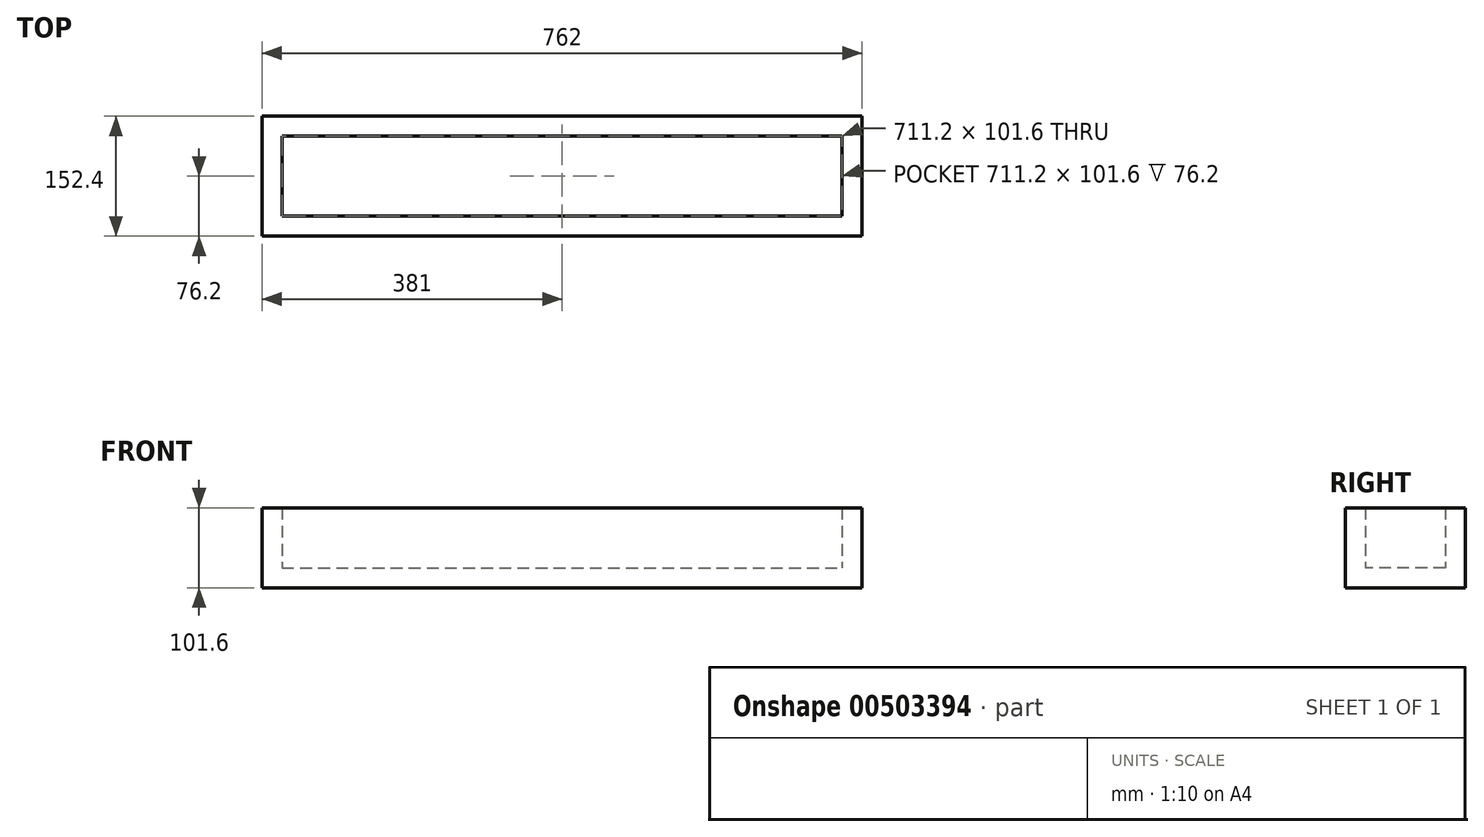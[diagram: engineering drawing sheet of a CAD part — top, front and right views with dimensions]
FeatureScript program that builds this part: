
annotation { "Feature Type Name" : "Feature", "Feature Type Description" : "" }
export const myFeature = defineFeature(function(context is Context, id is Id, definition is map)
    precondition{}
    {
        {
            var Q0;
            Q0=qCreatedBy(makeId("Top.planeOp"),FACE);
            var sketch = newSketch(context, id + "F0", { "sketchPlane" : qUnion([Q0])});
            skLineSegment(sketch, "E0.bottom", {"start": v(-381, 76.2) * mm, "end": v(381, 76.2) * mm});
            skLineSegment(sketch, "E0.top", {"start": v(-381, -76.2) * mm, "end": v(381, -76.2) * mm});
            skLineSegment(sketch, "E0.left", {"start": v(-381, 76.2) * mm, "end": v(-381, -76.2) * mm});
            skLineSegment(sketch, "E0.right", {"start": v(381, 76.2) * mm, "end": v(381, -76.2) * mm});
            skLineSegment(sketch, "E1", {"start": v(-381, 0) * mm, "end": v(381, 0) * mm, "construction": true});
            skSolve(sketch);
        }
        {
            var Q0;
            Q0 = qSketchRegion(id + "F0", true);
            extrude(context, id + "F1", {"entities" : qUnion([Q0]), "depth" : 101.6 * mm});
        }
        {
            var Q0;
            Q0=makeQuery(id+"F1.opExtrude","CAP_FACE",FACE,{"disambiguationData":[OSD([sQuery(id+"F0.wireOp",EDGE,"E0.bottom"),sQuery(id+"F0.wireOp",EDGE,"E0.top"),sQuery(id+"F0.wireOp",EDGE,"E0.left"),sQuery(id+"F0.wireOp",EDGE,"E0.right")])],"isStart":false});
            shell(context, id + "F2", {"entities" : qUnion([Q0]), "thickness" : 25.4 * mm});
        }
    });
